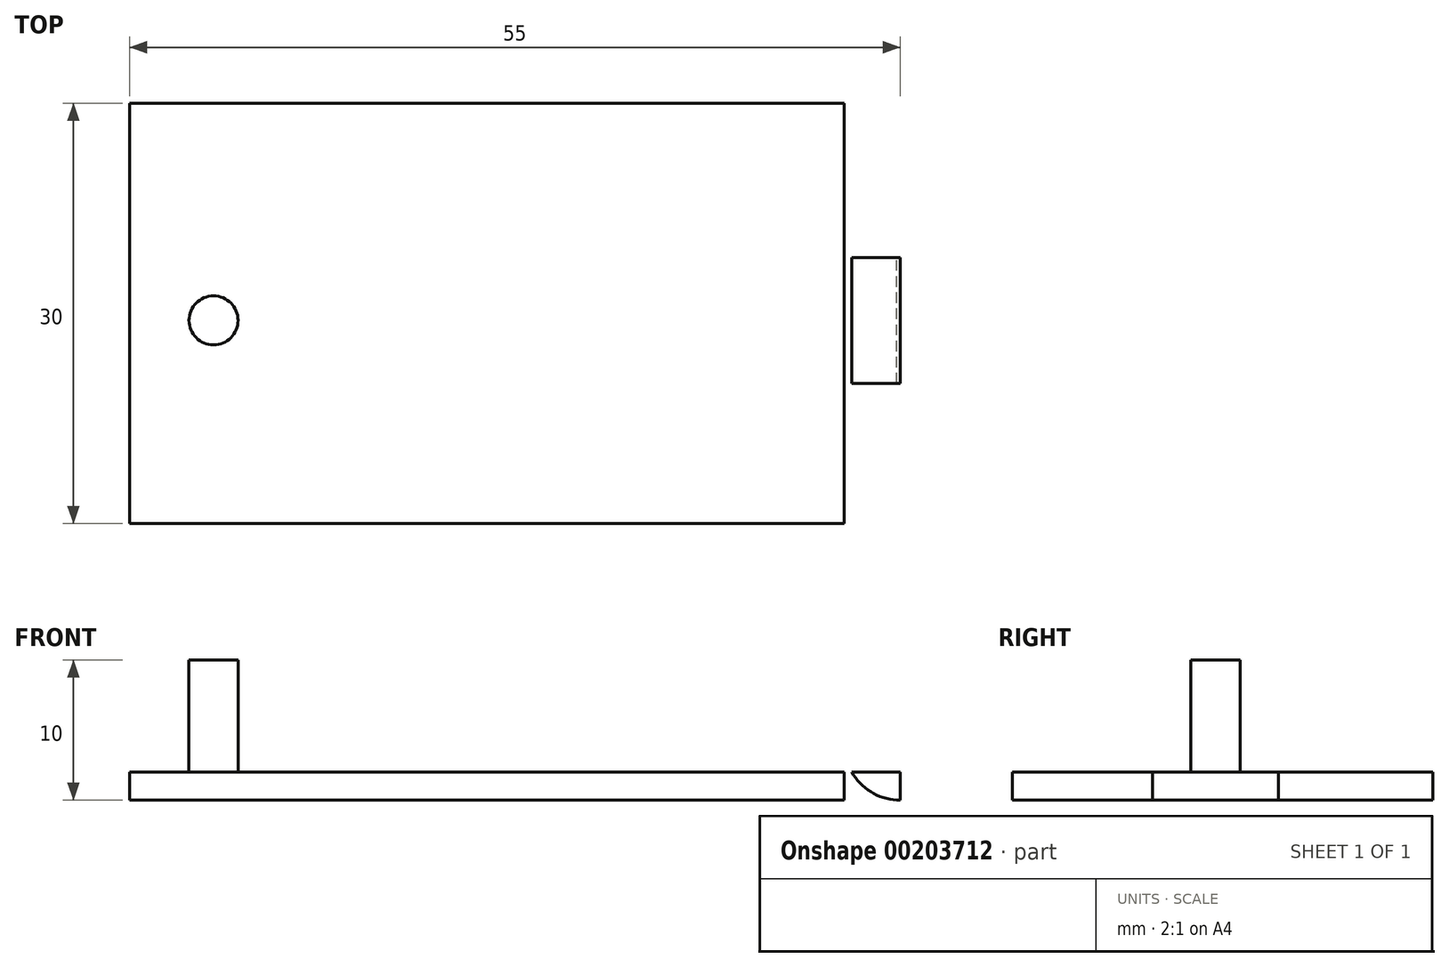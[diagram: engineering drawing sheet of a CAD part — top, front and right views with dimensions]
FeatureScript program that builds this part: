
annotation { "Feature Type Name" : "Feature", "Feature Type Description" : "" }
export const myFeature = defineFeature(function(context is Context, id is Id, definition is map)
    precondition{}
    {
        {
            var Q0;
            Q0=qCreatedBy(makeId("Front.planeOp"),FACE);
            var sketch = newSketch(context, id + "F0", { "sketchPlane" : qUnion([Q0])});
            skCircle(sketch, "E0", {"center": v(0, 0) * mm, "radius": 4 * mm});
            skCircle(sketch, "E1", {"center": v(0, 0) * mm, "radius": 1.5 * mm});
            skLineSegment(sketch, "E2.bottom", {"start": v(0, -4) * mm, "end": v(55, -4) * mm});
            skLineSegment(sketch, "E2.top", {"start": v(0, -2) * mm, "end": v(55, -2) * mm});
            skLineSegment(sketch, "E2.left", {"start": v(0, -4) * mm, "end": v(0, -2) * mm});
            skLineSegment(sketch, "E2.right", {"start": v(55, -4) * mm, "end": v(55, -2) * mm});
            skLineSegment(sketch, "E3", {"start": v(55, -2) * mm, "end": v(55, 0) * mm});
            skCircle(sketch, "E4", {"center": v(55, 0) * mm, "radius": 4 * mm});
            skCircle(sketch, "E5", {"center": v(55, 0) * mm, "radius": 2 * mm});
            skLineSegment(sketch, "E6", {"start": v(5, -4) * mm, "end": v(5, -8) * mm});
            skLineSegment(sketch, "E7", {"start": v(5, -8) * mm, "end": v(0, -4) * mm});
            skLineSegment(sketch, "E8", {"start": v(51, 0) * mm, "end": v(51, -4) * mm});
            skLineSegment(sketch, "E9", {"start": v(53.29, 3.6) * mm, "end": v(42.75, -2) * mm});
            skLineSegment(sketch, "E10", {"start": v(0, -2) * mm, "end": v(5, 2) * mm});
            skLineSegment(sketch, "E11", {"start": v(5, 2) * mm, "end": v(5, -2) * mm});
            skSolve(sketch);
        }
        {
            var Q0;
            {var subQ1=sQuery(id+"F0.wireOp",EDGE,"E0");var subQ3=sQuery(id+"F0.wireOp",EDGE,"E2.top");var subQ4=makeQuery(id+"F0.imprint","INTERSECT",VERTEX,{"derivedFrom":[subQ1,subQ3]});Q0=makeQuery(id+"F0.imprint","IMPRINT",FACE,{"disambiguationData":[TD([[makeQuery(id+"F0.imprint","IMPRINT",EDGE,{"disambiguationData":[TD([[subQ4,-1.0]])],"derivedFrom":subQ3}),-1.0]])]});}
            var Q1;
            {var subQ0=sQuery(id+"F0.wireOp",EDGE,"E2.left");Q1=makeQuery(id+"F0.imprint","IMPRINT",FACE,{"disambiguationData":[TD([[makeQuery(id+"F0.imprint","IMPRINT",EDGE,{"derivedFrom":subQ0}),-1.0]])]});}
            var Q2;
            {var subQ0=sQuery(id+"F0.wireOp",EDGE,"E2.right");Q2=makeQuery(id+"F0.imprint","IMPRINT",FACE,{"disambiguationData":[TD([[makeQuery(id+"F0.imprint","IMPRINT",EDGE,{"derivedFrom":subQ0}),1.0]])]});}
            var Q3;
            {var subQ1=sQuery(id+"F0.wireOp",EDGE,"E4");var subQ7=makeQuery(id+"F0.imprint","IMPRINT",VERTEX,{"derivedFrom":subQ1});Q3=makeQuery(id+"F0.imprint","IMPRINT",FACE,{"disambiguationData":[TD([[makeQuery(id+"F0.imprint","IMPRINT",EDGE,{"disambiguationData":[TD([[subQ7,1.0]])],"derivedFrom":subQ1}),-1.0]])]});}
            var Q4;
            {var subQ0=sQuery(id+"F0.wireOp",EDGE,"E4");var subQ1=makeQuery(id+"F0.imprint","IMPRINT",VERTEX,{"derivedFrom":subQ0});Q4=makeQuery(id+"F0.imprint","IMPRINT",FACE,{"disambiguationData":[TD([[makeQuery(id+"F0.imprint","IMPRINT",EDGE,{"disambiguationData":[TD([[subQ1,1.0]])],"derivedFrom":subQ0}),1.0]])]});}
            var Q5;
            {var subQ0=sQuery(id+"F0.wireOp",EDGE,"E2.right");var subQ1=sQuery(id+"F0.wireOp",EDGE,"E2.bottom");var subQ2=makeQuery(id+"F0.imprint","INTERSECT",VERTEX,{"derivedFrom":[subQ1,subQ0]});Q5=makeQuery(id+"F0.imprint","IMPRINT",FACE,{"disambiguationData":[TD([[makeQuery(id+"F0.imprint","IMPRINT",EDGE,{"disambiguationData":[TD([[subQ2,1.0]])],"derivedFrom":subQ1}),1.0]])]});}
            extrude(context, id + "F1", {"entities" : qUnion([Q0, Q1, Q2, Q3, Q4, Q5]), "depth" : 20 * mm, "hasSecondDirection" : true, "secondDirectionOppositeDirection" : false, "secondDirectionDepth" : 11 * mm});
        }
        {
            var Q0;
            {var subQ0=sQuery(id+"F0.wireOp",EDGE,"E2.bottom");Q0=makeQuery(id+"F0amyIbCvxJC7EA_1.boolean.opBoolean","MERGE",FACE,{"derivedFrom":[makeQuery(id+"FixQ7C7vZYy5nc9_1.boolean.opBoolean","MERGE",FACE,{"derivedFrom":[makeQuery(id+"F1.opExtrude","SWEPT_FACE",FACE,{"disambiguationData":[OSD([subQ0])]}),makeQuery(id+"FixQ7C7vZYy5nc9_1.opExtrude","SWEPT_FACE",FACE,{"disambiguationData":[OSD([subQ0])]})]}),makeQuery(id+"F0amyIbCvxJC7EA_1.opExtrude","SWEPT_FACE",FACE,{"disambiguationData":[OSD([subQ0])]})]});}
            var sketch = newSketch(context, id + "F2", { "sketchPlane" : qUnion([Q0])});
            skLineSegment(sketch, "E12", {"start": v(6, 20) * mm, "end": v(6, 15.5) * mm});
            skCircle(sketch, "E13", {"center": v(6, 15.5) * mm, "radius": 1.75 * mm});
            skSolve(sketch);
        }
        {
            var Q0;
            {var subQ5=sQuery(id+"F0.wireOp",EDGE,"E2.bottom");var subQ6=makeQuery(id+"F0.imprint","INTERSECT",VERTEX,{"derivedFrom":[subQ5,sQuery(id+"F0.wireOp",EDGE,"E6")]});Q0=makeQuery(id+"F0.imprint","IMPRINT",FACE,{"disambiguationData":[TD([[makeQuery(id+"F0.imprint","IMPRINT",EDGE,{"disambiguationData":[TD([[subQ6,-1.0]])],"derivedFrom":subQ5}),1.0]])]});}
            var Q1;
            {var subQ0=sQuery(id+"F0.wireOp",EDGE,"E2.left");Q1=makeQuery(id+"F0.imprint","IMPRINT",FACE,{"disambiguationData":[TD([[makeQuery(id+"F0.imprint","IMPRINT",EDGE,{"derivedFrom":subQ0}),-1.0]])]});}
            extrude(context, id + "F3", {"entities" : qUnion([Q0, Q1]), "operationType" : NewBodyOperationType.ADD, "depth" : 30 * mm});
        }
        {
            var Q0;
            Q0=makeQuery(id+"F2.imprint","IMPRINT",FACE,{"disambiguationData":[TD([[makeQuery(id+"F2.imprint","IMPRINT",EDGE,{"derivedFrom":sQuery(id+"F2.wireOp",EDGE,"E13")}),1.0]])]});
            extrude(context, id + "F4", {"entities" : qUnion([Q0]), "operationType" : NewBodyOperationType.ADD, "oppositeDirection" : true, "depth" : 10 * mm});
        }
    });
